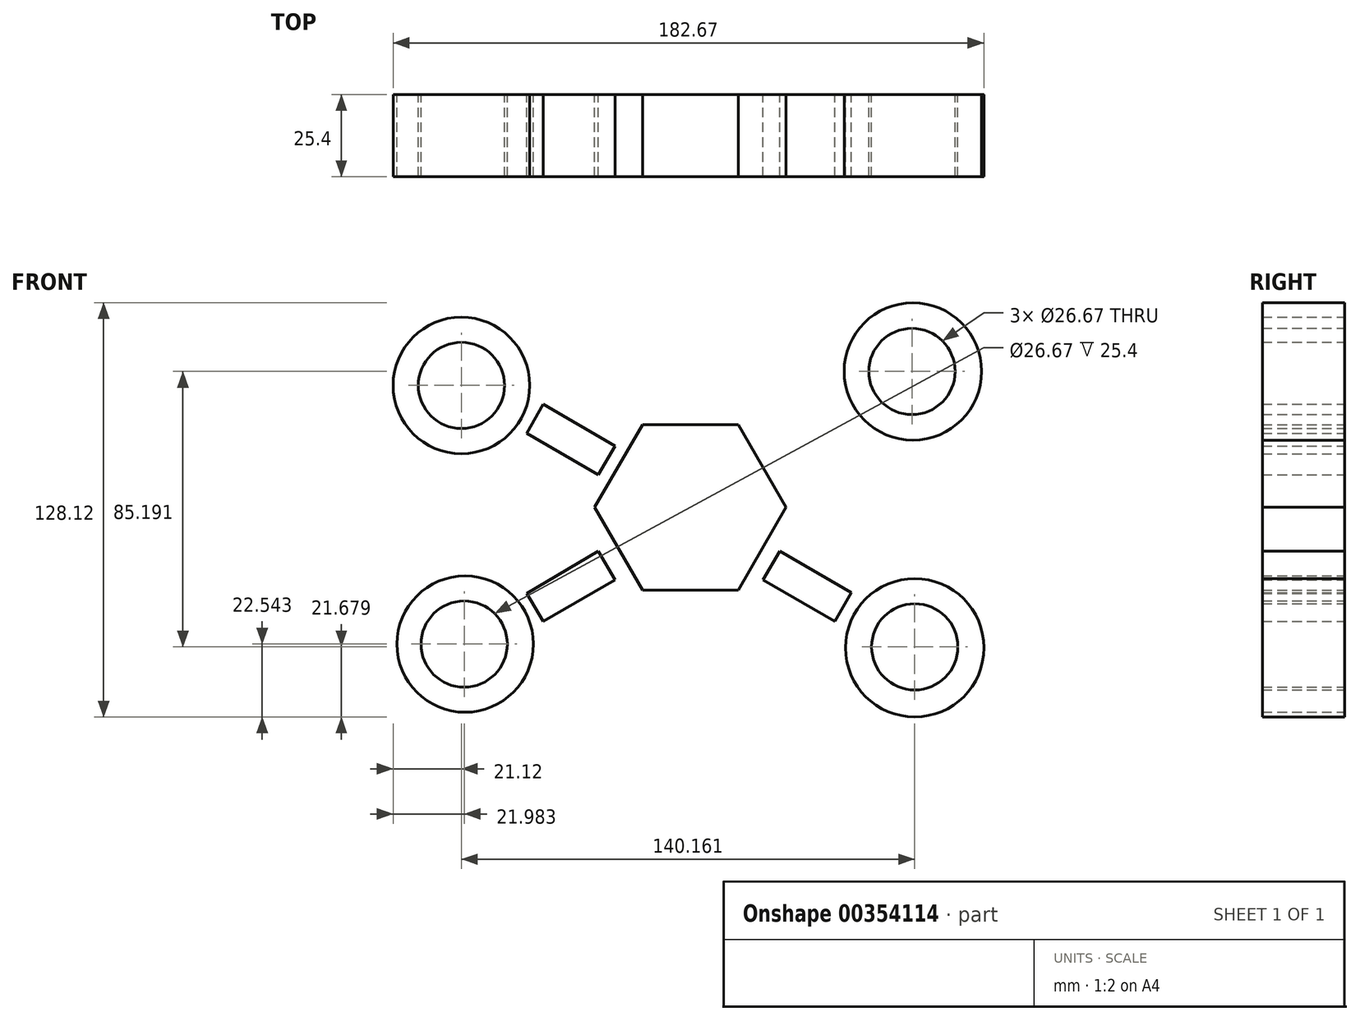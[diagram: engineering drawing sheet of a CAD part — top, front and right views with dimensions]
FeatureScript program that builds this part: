
annotation { "Feature Type Name" : "Feature", "Feature Type Description" : "" }
export const myFeature = defineFeature(function(context is Context, id is Id, definition is map)
    precondition{}
    {
        {
            var Q0;
            Q0=qCreatedBy(makeId("Front.planeOp"),FACE);
            var sketch = newSketch(context, id + "F0", { "sketchPlane" : qUnion([Q0])});
            skCircle(sketch, "E0.cCircle", {"center": v(0, 0) * mm, "radius": 25.61 * mm, "construction": true});
            skLineSegment(sketch, "E0.0", {"start": v(14.79, -25.61) * mm, "end": v(-14.79, -25.61) * mm});
            skLineSegment(sketch, "E0.1", {"start": v(-14.79, -25.61) * mm, "end": v(-29.58, 0) * mm});
            skLineSegment(sketch, "E0.2", {"start": v(-29.58, 0) * mm, "end": v(-14.79, 25.61) * mm});
            skLineSegment(sketch, "E0.3", {"start": v(-14.79, 25.61) * mm, "end": v(14.79, 25.61) * mm});
            skLineSegment(sketch, "E0.4", {"start": v(14.79, 25.61) * mm, "end": v(29.58, 0) * mm});
            skLineSegment(sketch, "E0.5", {"start": v(29.58, 0) * mm, "end": v(14.79, -25.61) * mm});
            skPoint(sketch, "E0.0.midPoint", {"position": v(0, -25.61) * mm});
            skLineSegment(sketch, "E1", {"start": v(-23.31, 19) * mm, "end": v(-28.5, 10.07) * mm});
            skLineSegment(sketch, "E2", {"start": v(-28.5, 10.07) * mm, "end": v(-50.53, 22.87) * mm});
            skLineSegment(sketch, "E3", {"start": v(-50.53, 22.87) * mm, "end": v(-28.5, 10.07) * mm});
            skLineSegment(sketch, "E4", {"start": v(-23.31, 19) * mm, "end": v(-45.5, 31.88) * mm});
            skLineSegment(sketch, "E5", {"start": v(-45.5, 31.88) * mm, "end": v(-50.53, 22.87) * mm});
            skLineSegment(sketch, "E6", {"start": v(27.63, 10.07) * mm, "end": v(49.8, 22.87) * mm});
            skLineSegment(sketch, "E7", {"start": v(49.8, 22.87) * mm, "end": v(27.63, 10.07) * mm});
            skLineSegment(sketch, "E8", {"start": v(27.63, 10.07) * mm, "end": v(22.48, 19) * mm});
            skLineSegment(sketch, "E9", {"start": v(22.48, 19) * mm, "end": v(44.8, 31.88) * mm});
            skLineSegment(sketch, "E10", {"start": v(44.8, 31.88) * mm, "end": v(49.8, 22.87) * mm});
            skLineSegment(sketch, "E11", {"start": v(-28.5, -13.53) * mm, "end": v(-23.31, -22.5) * mm});
            skLineSegment(sketch, "E12", {"start": v(-23.31, -22.5) * mm, "end": v(-45.5, -35.32) * mm});
            skLineSegment(sketch, "E13", {"start": v(-45.5, -35.32) * mm, "end": v(-50.53, -26.62) * mm});
            skLineSegment(sketch, "E14", {"start": v(-50.53, -26.62) * mm, "end": v(-28.5, -13.53) * mm});
            skLineSegment(sketch, "E15", {"start": v(22.48, -22.5) * mm, "end": v(27.63, -13.58) * mm});
            skLineSegment(sketch, "E16", {"start": v(27.63, -13.58) * mm, "end": v(49.8, -26.37) * mm});
            skLineSegment(sketch, "E17", {"start": v(49.8, -26.37) * mm, "end": v(44.63, -35.32) * mm});
            skLineSegment(sketch, "E18", {"start": v(44.63, -35.32) * mm, "end": v(22.48, -22.5) * mm});
            skCircle(sketch, "E19", {"center": v(-70.8, 37.7) * mm, "radius": 21.12 * mm});
            skCircle(sketch, "E20", {"center": v(-69.65, -42.3) * mm, "radius": 21.08 * mm});
            skCircle(sketch, "E21", {"center": v(69.36, -43.46) * mm, "radius": 21.4 * mm});
            skCircle(sketch, "E22", {"center": v(68.79, 42.02) * mm, "radius": 21.25 * mm});
            skSolve(sketch);
        }
        {
            var Q0;
            Q0=makeQuery(id+"F0.imprint","IMPRINT",FACE,{"disambiguationData":[TD([[makeQuery(id+"F0.imprint","IMPRINT",EDGE,{"derivedFrom":sQuery(id+"F0.wireOp",EDGE,"E19")}),1.0]])]});
            var sketch = newSketch(context, id + "F1", { "sketchPlane" : qUnion([Q0])});
            skCircle(sketch, "E23", {"center": v(-70.8, 37.7) * mm, "radius": 14.03 * mm});
            skCircle(sketch, "E24", {"center": v(-69.94, -42.3) * mm, "radius": 12.87 * mm});
            skCircle(sketch, "E25", {"center": v(69.36, -43.17) * mm, "radius": 13.9 * mm});
            skCircle(sketch, "E26", {"center": v(68.5, 42.02) * mm, "radius": 14.22 * mm});
            skSolve(sketch);
        }
        {
            var Q0;
            Q0=makeQuery(id+"F0.imprint","IMPRINT",FACE,{"disambiguationData":[TD([[makeQuery(id+"F0.imprint","IMPRINT",EDGE,{"derivedFrom":sQuery(id+"F0.wireOp",EDGE,"E1")}),-1.0]])]});
            var Q1;
            Q1=makeQuery(id+"F0.imprint","IMPRINT",FACE,{"disambiguationData":[TD([[makeQuery(id+"F0.imprint","IMPRINT",EDGE,{"derivedFrom":sQuery(id+"F0.wireOp",EDGE,"E0.0")}),-1.0]])]});
            var Q2;
            Q2=makeQuery(id+"F0.imprint","IMPRINT",FACE,{"disambiguationData":[TD([[makeQuery(id+"F0.imprint","IMPRINT",EDGE,{"derivedFrom":sQuery(id+"F0.wireOp",EDGE,"E7")}),-1.0]])]});
            var Q3;
            Q3=makeQuery(id+"F0.imprint","IMPRINT",FACE,{"disambiguationData":[TD([[makeQuery(id+"F0.imprint","IMPRINT",EDGE,{"derivedFrom":sQuery(id+"F0.wireOp",EDGE,"E22")}),1.0]])]});
            var Q4;
            Q4=makeQuery(id+"F0.imprint","IMPRINT",FACE,{"disambiguationData":[TD([[makeQuery(id+"F0.imprint","IMPRINT",EDGE,{"derivedFrom":sQuery(id+"F0.wireOp",EDGE,"E20")}),1.0]])]});
            var Q5;
            Q5=makeQuery(id+"F0.imprint","IMPRINT",FACE,{"disambiguationData":[TD([[makeQuery(id+"F0.imprint","IMPRINT",EDGE,{"derivedFrom":sQuery(id+"F0.wireOp",EDGE,"E19")}),1.0]])]});
            var Q6;
            Q6=makeQuery(id+"F0.imprint","IMPRINT",FACE,{"disambiguationData":[TD([[makeQuery(id+"F0.imprint","IMPRINT",EDGE,{"derivedFrom":sQuery(id+"F0.wireOp",EDGE,"E11")}),-1.0]])]});
            var Q7;
            Q7=makeQuery(id+"F0.imprint","IMPRINT",FACE,{"disambiguationData":[TD([[makeQuery(id+"F0.imprint","IMPRINT",EDGE,{"derivedFrom":sQuery(id+"F0.wireOp",EDGE,"E15")}),-1.0]])]});
            var Q8;
            Q8=makeQuery(id+"F0.imprint","IMPRINT",FACE,{"disambiguationData":[TD([[makeQuery(id+"F0.imprint","IMPRINT",EDGE,{"derivedFrom":sQuery(id+"F0.wireOp",EDGE,"E21")}),1.0]])]});
            extrude(context, id + "F2", {"entities" : qUnion([Q0, Q1, Q2, Q3, Q4, Q5, Q6, Q7, Q8]), "depth" : 25.4 * mm});
        }
        {
            var Q0;
            Q0=sQuery(id+"F1.wireOp",VERTEX,"E23.center");
            var Q1;
            Q1=sQuery(id+"F1.wireOp",VERTEX,"E24.center");
            var Q2;
            Q2=sQuery(id+"F1.wireOp",VERTEX,"E26.center");
            var Q3;
            Q3=sQuery(id+"F1.wireOp",VERTEX,"E25.center");
            var Q4;
            Q4=makeQuery(id+"F2.opExtrude","SWEPT_BODY",BODY,{"disambiguationData":[OSD([sQuery(id+"F0.wireOp",EDGE,"E19")])]});
            var Q5;
            Q5=makeQuery(id+"F2.opExtrude","SWEPT_BODY",BODY,{"disambiguationData":[OSD([sQuery(id+"F0.wireOp",EDGE,"E20")])]});
            var Q6;
            Q6=makeQuery(id+"F2.opExtrude","SWEPT_BODY",BODY,{"disambiguationData":[OSD([sQuery(id+"F0.wireOp",EDGE,"E22")])]});
            var Q7;
            Q7=makeQuery(id+"F2.opExtrude","SWEPT_BODY",BODY,{"disambiguationData":[OSD([sQuery(id+"F0.wireOp",EDGE,"E21")])]});
            hole(context, id + "F3", {"style" : HoleStyle.SIMPLE, "endStyle" : HoleEndStyle.THROUGH, "oppositeDirection" : true, "holeDiameter" : 26.67 * mm, "isTappedThrough" : true, "tappedDepth" : 12.7 * mm, "tapClearance" : 3, "startFromSketch" : true, "locations" : qUnion([Q0, Q1, Q2, Q3]), "scope" : qUnion([Q4, Q5, Q6, Q7])});
        }
    });
